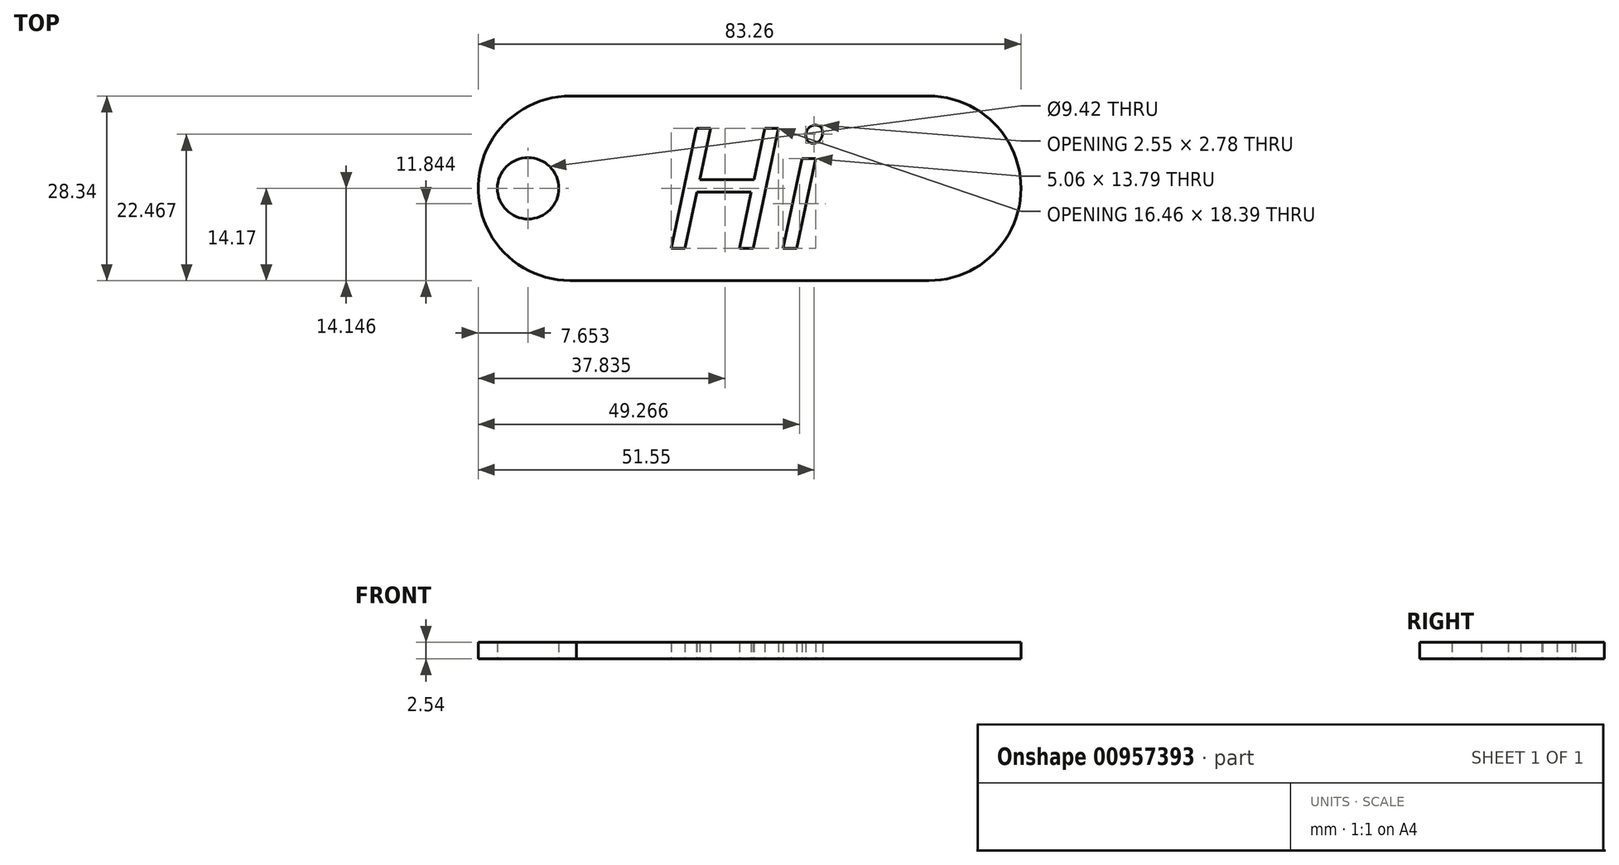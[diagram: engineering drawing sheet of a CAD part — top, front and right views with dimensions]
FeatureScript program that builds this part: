
annotation { "Feature Type Name" : "Feature", "Feature Type Description" : "" }
export const myFeature = defineFeature(function(context is Context, id is Id, definition is map)
    precondition{}
    {
        {
            var Q0;
            Q0=qCreatedBy(makeId("Top.planeOp"),FACE);
            var sketch = newSketch(context, id + "F0", { "sketchPlane" : qUnion([Q0])});
            skCircle(sketch, "E0", {"center": v(-27.47, 0) * mm, "radius": 14.17 * mm});
            skCircle(sketch, "E1.MirrorC", {"center": v(27.47, 0) * mm, "radius": 14.17 * mm});
            skLineSegment(sketch, "E2", {"start": v(-27.47, 14.17) * mm, "end": v(27.47, 14.17) * mm});
            skLineSegment(sketch, "E3", {"start": v(-28.39, -14.14) * mm, "end": v(27.47, -14.17) * mm});
            skCircle(sketch, "E4", {"center": v(-33.98, 0) * mm, "radius": 4.7 * mm});
            skText(sketch, "E5", { "text": "Hi ", "fontName": "OpenSans-Italic.ttf"});
            const initialGuessF0  = {"E5": [-0.01311, -0.00922, 1, 0, 0.01855]};
            skSetInitialGuess(sketch, initialGuessF0);
            skSolve(sketch);
        }
        {
            var Q0;
            Q0 = qSketchRegion(id + "F0", true);
            extrude(context, id + "F1", {"entities" : qUnion([Q0]), "depth" : 2.54 * mm, "offsetDistance" : 25.4 * mm});
        }
    });
